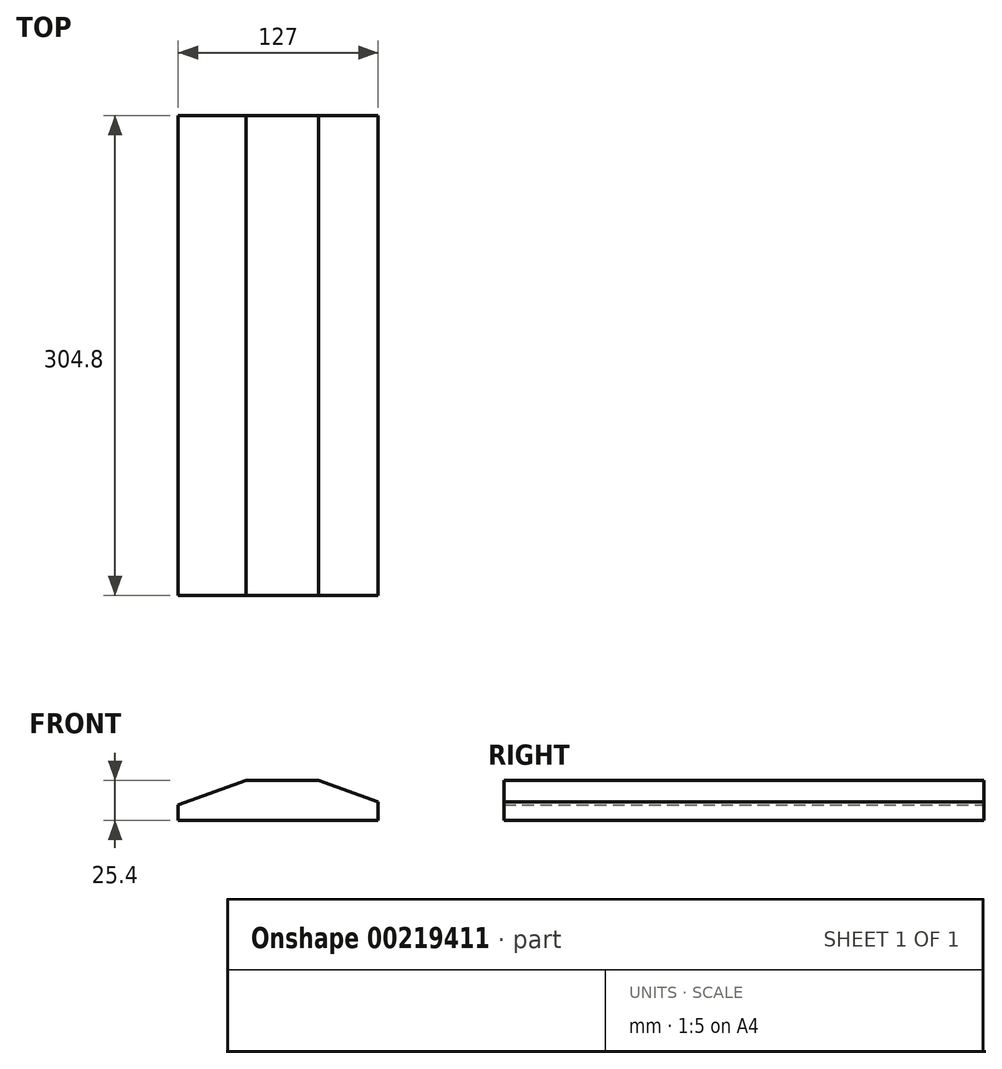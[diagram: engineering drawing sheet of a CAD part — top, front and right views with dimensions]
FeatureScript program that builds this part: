
annotation { "Feature Type Name" : "Feature", "Feature Type Description" : "" }
export const myFeature = defineFeature(function(context is Context, id is Id, definition is map)
    precondition{}
    {
        {
            var Q0;
            Q0=qCreatedBy(makeId("Front.planeOp"),FACE);
            var sketch = newSketch(context, id + "F0", { "sketchPlane" : qUnion([Q0])});
            skLineSegment(sketch, "E0.bottom", {"start": v(-63.5, -12.7) * mm, "end": v(63.5, -12.7) * mm});
            skLineSegment(sketch, "E0.top", {"start": v(-20.54, 12.7) * mm, "end": v(25.59, 12.7) * mm});
            skLineSegment(sketch, "E0.left", {"start": v(-63.5, -12.7) * mm, "end": v(-63.5, -2.94) * mm});
            skLineSegment(sketch, "E0.right", {"start": v(63.5, -12.7) * mm, "end": v(63.5, -1.1) * mm});
            skPoint(sketch, "E0.middle", {"position": v(0, 0) * mm});
            skLineSegment(sketch, "E1", {"start": v(-20.54, 12.7) * mm, "end": v(-63.5, -2.94) * mm});
            skLineSegment(sketch, "E2", {"start": v(25.59, 12.7) * mm, "end": v(63.5, -1.1) * mm});
            skPoint(sketch, "E3.orphan", {"position": v(-63.5, 12.7) * mm});
            skPoint(sketch, "E4.orphan", {"position": v(63.5, 12.7) * mm});
            skSolve(sketch);
        }
        {
            var Q0;
            Q0=makeQuery(id+"F0.imprint","IMPRINT",FACE,{"disambiguationData":[TD([[makeQuery(id+"F0.imprint","IMPRINT",EDGE,{"derivedFrom":sQuery(id+"F0.wireOp",EDGE,"E0.bottom")}),1.0]])]});
            extrude(context, id + "F1", {"entities" : qUnion([Q0]), "endBound" : BoundingType.SYMMETRIC, "depth" : 304.8 * mm});
        }
    });
